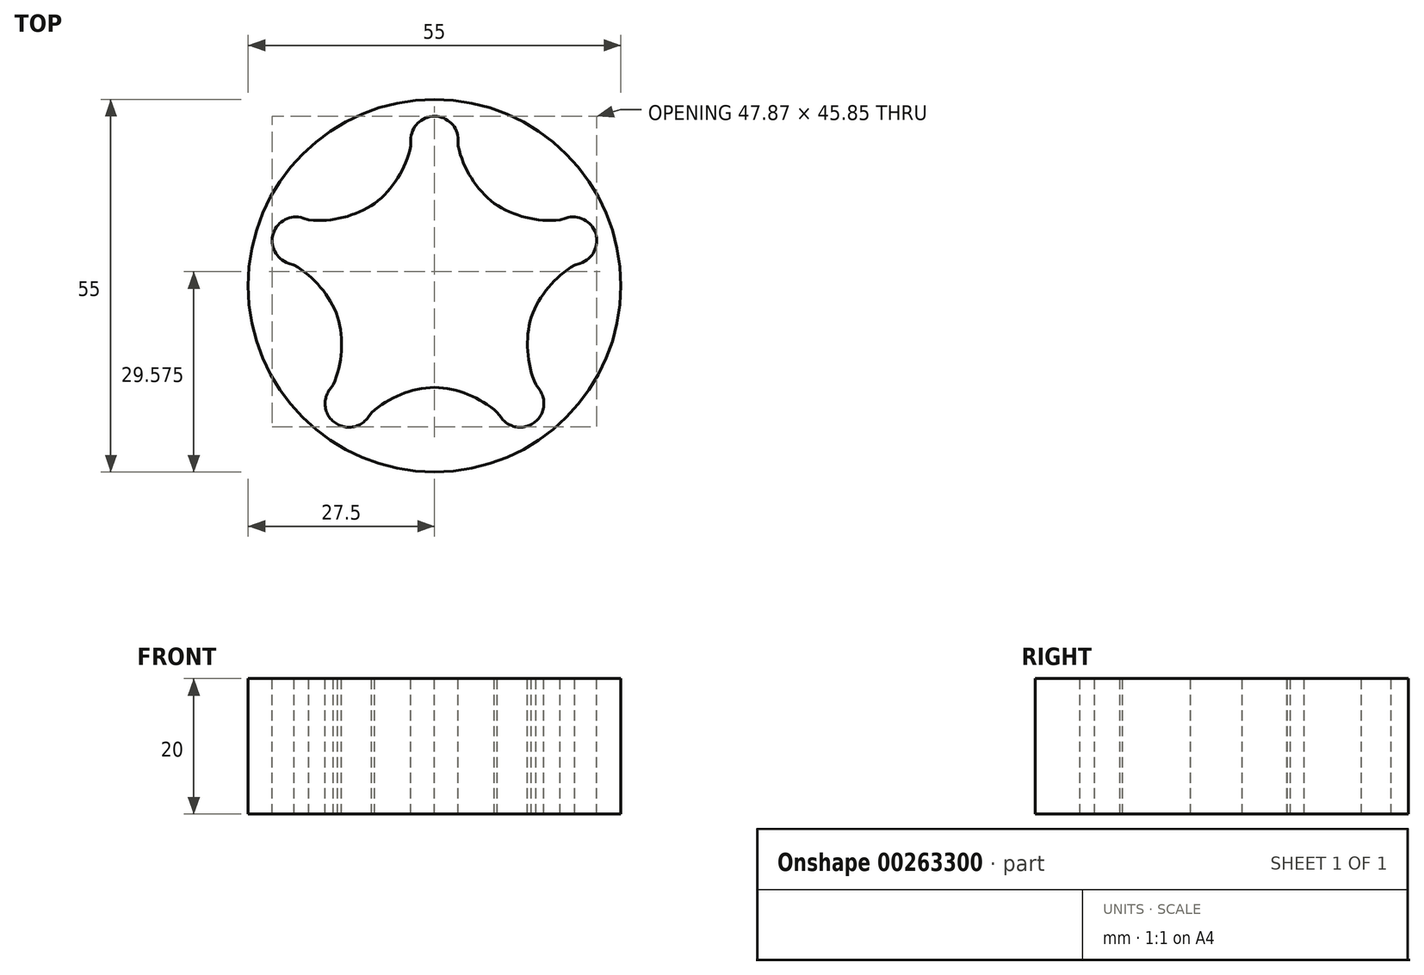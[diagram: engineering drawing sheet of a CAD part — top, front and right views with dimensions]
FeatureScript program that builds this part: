
annotation { "Feature Type Name" : "Feature", "Feature Type Description" : "" }
export const myFeature = defineFeature(function(context is Context, id is Id, definition is map)
    precondition{}
    {
        {
            var Q0;
            Q0=qCreatedBy(makeId("Top.planeOp"),FACE);
            var sketch = newSketch(context, id + "F0", { "sketchPlane" : qUnion([Q0])});
            skCircle(sketch, "E0", {"center": v(0, -5) * mm, "radius": 27.5 * mm});
            skLineSegment(sketch, "E1", {"start": v(0, -5) * mm, "end": v(-57.06, 13.54) * mm});
            skLineSegment(sketch, "E2", {"start": v(0, -5) * mm, "end": v(52.71, 12.13) * mm});
            skLineSegment(sketch, "E3", {"start": v(0, -5) * mm, "end": v(23.23, -36.98) * mm});
            skLineSegment(sketch, "E4", {"start": v(0, -5) * mm, "end": v(-21.37, -34.42) * mm});
            skPoint(sketch, "E5", {"position": v(0, 16.5) * mm});
            skArc(sketch, "E6", {"start": v(-3.5, 16.5) * mm, "mid": v(0, 20) * mm, "end": v(3.5, 16.5) * mm});
            skArc(sketch, "E7.MirrorCS", {"start": v(9.8, -24.45) * mm, "mid": v(14.7, -25.23) * mm, "end": v(15.47, -20.34) * mm});
            skArc(sketch, "E8.MirrorCS", {"start": v(-21.53, -1.68) * mm, "mid": v(-23.78, 2.73) * mm, "end": v(-19.37, 4.97) * mm});
            skArc(sketch, "E9.MirrorCS", {"start": v(21.53, -1.68) * mm, "mid": v(23.78, 2.73) * mm, "end": v(19.37, 4.97) * mm});
            skArc(sketch, "E10.MirrorCS", {"start": v(-9.8, -24.45) * mm, "mid": v(-14.7, -25.23) * mm, "end": v(-15.47, -20.34) * mm});
            skPoint(sketch, "E11", {"position": v(0, -20) * mm});
            skSolve(sketch);
        }
        {
            var Q0;
            Q0=qCreatedBy(makeId("Top.planeOp"),FACE);
            var sketch = newSketch(context, id + "F1", { "sketchPlane" : qUnion([Q0])});
            skPoint(sketch, "E12", {"position": v(0, -9.66) * mm});
            skPoint(sketch, "E13", {"position": v(11.67, -21.33) * mm});
            skPoint(sketch, "E14", {"position": v(-11.67, -21.33) * mm});
            skPoint(sketch, "E15.MirrorP", {"position": v(14.58, -9.74) * mm});
            skPoint(sketch, "E16", {"position": v(0, -20) * mm});
            skPoint(sketch, "E17", {"position": v(9.8, -24.45) * mm});
            skPoint(sketch, "E18", {"position": v(-9.8, -24.45) * mm});
            skPoint(sketch, "E19", {"position": v(-18.52, 4.7) * mm});
            skPoint(sketch, "E20", {"position": v(-8.82, 7.14) * mm});
            skArc(sketch, "E21", {"start": v(-18.52, 4.7) * mm, "mid": v(-13.46, 5.08) * mm, "end": v(-8.82, 7.14) * mm});
            skLineSegment(sketch, "E22", {"start": v(-18.52, 4.7) * mm, "end": v(-19.37, 4.97) * mm});
            skLineSegment(sketch, "E23.MirrorCS", {"start": v(-20.69, -1.96) * mm, "end": v(-21.53, -1.68) * mm});
            skArc(sketch, "E24.MirrorCS", {"start": v(-20.69, -1.96) * mm, "mid": v(-16.81, -5.24) * mm, "end": v(-14.27, -9.64) * mm});
            skArc(sketch, "E25.MirrorCS", {"start": v(9.29, -23.74) * mm, "mid": v(4.97, -21.06) * mm, "end": v(0, -20) * mm});
            skLineSegment(sketch, "E26.MirrorCS", {"start": v(9.29, -23.74) * mm, "end": v(9.8, -24.45) * mm});
            skArc(sketch, "E27.MirrorCS", {"start": v(-3.5, 15.61) * mm, "mid": v(-5.43, 10.92) * mm, "end": v(-8.82, 7.14) * mm});
            skLineSegment(sketch, "E28.MirrorCS", {"start": v(-3.5, 15.61) * mm, "end": v(-3.5, 16.5) * mm});
            skArc(sketch, "E29.MirrorCS", {"start": v(3.5, 15.61) * mm, "mid": v(5.43, 10.92) * mm, "end": v(8.82, 7.14) * mm});
            skArc(sketch, "E30.MirrorCS", {"start": v(18.52, 4.7) * mm, "mid": v(13.46, 5.08) * mm, "end": v(8.82, 7.14) * mm});
            skLineSegment(sketch, "E31.MirrorCS", {"start": v(18.52, 4.7) * mm, "end": v(19.37, 4.97) * mm});
            skLineSegment(sketch, "E32.MirrorCS", {"start": v(3.5, 15.61) * mm, "end": v(3.5, 16.5) * mm});
            skArc(sketch, "E33.MirrorCS", {"start": v(20.69, -1.96) * mm, "mid": v(16.81, -5.24) * mm, "end": v(14.27, -9.64) * mm});
            skArc(sketch, "E34.MirrorCS", {"start": v(14.95, -19.62) * mm, "mid": v(13.74, -14.69) * mm, "end": v(14.27, -9.64) * mm});
            skLineSegment(sketch, "E35.MirrorCS", {"start": v(14.95, -19.62) * mm, "end": v(15.47, -20.34) * mm});
            skLineSegment(sketch, "E36.MirrorCS", {"start": v(20.69, -1.96) * mm, "end": v(21.53, -1.68) * mm});
            skArc(sketch, "E37.MirrorCS", {"start": v(-14.95, -19.62) * mm, "mid": v(-13.74, -14.69) * mm, "end": v(-14.27, -9.64) * mm});
            skLineSegment(sketch, "E38.MirrorCS", {"start": v(-14.95, -19.62) * mm, "end": v(-15.47, -20.34) * mm});
            skArc(sketch, "E39.MirrorCS", {"start": v(-9.29, -23.74) * mm, "mid": v(-4.97, -21.06) * mm, "end": v(0, -20) * mm});
            skLineSegment(sketch, "E40.MirrorCS", {"start": v(-9.29, -23.74) * mm, "end": v(-9.8, -24.45) * mm});
            skArc(sketch, "E41", {"start": v(9.8, -24.45) * mm, "mid": v(14.7, -25.23) * mm, "end": v(15.47, -20.34) * mm});
            skArc(sketch, "E42", {"start": v(21.53, -1.68) * mm, "mid": v(23.78, 2.73) * mm, "end": v(19.37, 4.97) * mm});
            skArc(sketch, "E43", {"start": v(3.5, 16.5) * mm, "mid": v(0, 20) * mm, "end": v(-3.5, 16.5) * mm});
            skArc(sketch, "E44", {"start": v(-19.37, 4.97) * mm, "mid": v(-23.78, 2.73) * mm, "end": v(-21.53, -1.68) * mm});
            skArc(sketch, "E45", {"start": v(-15.47, -20.34) * mm, "mid": v(-14.7, -25.23) * mm, "end": v(-9.8, -24.45) * mm});
            skSolve(sketch);
        }
        {
            var Q0;
            Q0 = qSketchRegion(id + "F1", true);
            extrude(context, id + "F2", {"entities" : qUnion([Q0]), "depth" : 25 * mm});
        }
        {
            var Q0;
            {var subQ1=sQuery(id+"F0.wireOp",EDGE,"E1");var subQ6=makeQuery(id+"F0.imprint","IMPRINT",VERTEX,{"derivedFrom":subQ1});Q0=makeQuery(id+"F0.imprint","IMPRINT",FACE,{"disambiguationData":[TD([[makeQuery(id+"F0.imprint","IMPRINT",EDGE,{"disambiguationData":[TD([[subQ6,-1.0]])],"derivedFrom":subQ1}),1.0]])]});}
            var Q1;
            {var subQ1=sQuery(id+"F0.wireOp",EDGE,"E1");var subQ4=makeQuery(id+"F0.imprint","IMPRINT",VERTEX,{"derivedFrom":subQ1});Q1=makeQuery(id+"F0.imprint","IMPRINT",FACE,{"disambiguationData":[TD([[makeQuery(id+"F0.imprint","IMPRINT",EDGE,{"disambiguationData":[TD([[subQ4,-1.0]])],"derivedFrom":subQ1}),-1.0]])]});}
            var Q2;
            {var subQ1=sQuery(id+"F0.wireOp",EDGE,"E2");var subQ6=makeQuery(id+"F0.imprint","IMPRINT",VERTEX,{"derivedFrom":subQ1});Q2=makeQuery(id+"F0.imprint","IMPRINT",FACE,{"disambiguationData":[TD([[makeQuery(id+"F0.imprint","IMPRINT",EDGE,{"disambiguationData":[TD([[subQ6,-1.0]])],"derivedFrom":subQ1}),-1.0]])]});}
            var Q3;
            {var subQ0=sQuery(id+"F0.wireOp",EDGE,"E3");var subQ3=makeQuery(id+"F0.imprint","IMPRINT",VERTEX,{"derivedFrom":subQ0});Q3=makeQuery(id+"F0.imprint","IMPRINT",FACE,{"disambiguationData":[TD([[makeQuery(id+"F0.imprint","IMPRINT",EDGE,{"disambiguationData":[TD([[subQ3,-1.0]])],"derivedFrom":subQ0}),-1.0]])]});}
            extrude(context, id + "F3", {"entities" : qUnion([Q0, Q1, Q2, Q3]), "operationType" : NewBodyOperationType.ADD, "depth" : 20 * mm});
        }
        {
            var Q0;
            Q0=makeQuery(id+"F2.opExtrude","CAP_FACE",FACE,{"disambiguationData":[OSD([sQuery(id+"F1.wireOp",EDGE,"E23.MirrorCS"),sQuery(id+"F1.wireOp",EDGE,"E24.MirrorCS"),sQuery(id+"F1.wireOp",EDGE,"E25.MirrorCS"),sQuery(id+"F1.wireOp",EDGE,"E26.MirrorCS"),sQuery(id+"F1.wireOp",EDGE,"E29.MirrorCS"),sQuery(id+"F1.wireOp",EDGE,"E30.MirrorCS"),sQuery(id+"F1.wireOp",EDGE,"E31.MirrorCS"),sQuery(id+"F1.wireOp",EDGE,"E32.MirrorCS"),sQuery(id+"F1.wireOp",EDGE,"E33.MirrorCS"),sQuery(id+"F1.wireOp",EDGE,"E34.MirrorCS"),sQuery(id+"F1.wireOp",EDGE,"E35.MirrorCS"),sQuery(id+"F1.wireOp",EDGE,"E36.MirrorCS"),sQuery(id+"F1.wireOp",EDGE,"E21"),sQuery(id+"F1.wireOp",EDGE,"E27.MirrorCS"),sQuery(id+"F1.wireOp",EDGE,"E28.MirrorCS"),sQuery(id+"F1.wireOp",EDGE,"E22"),sQuery(id+"F1.wireOp",EDGE,"E37.MirrorCS"),sQuery(id+"F1.wireOp",EDGE,"E38.MirrorCS"),sQuery(id+"F1.wireOp",EDGE,"E39.MirrorCS"),sQuery(id+"F1.wireOp",EDGE,"E40.MirrorCS"),sQuery(id+"F1.wireOp",EDGE,"E41"),sQuery(id+"F1.wireOp",EDGE,"E42"),sQuery(id+"F1.wireOp",EDGE,"E43"),sQuery(id+"F1.wireOp",EDGE,"E44"),sQuery(id+"F1.wireOp",EDGE,"E45")])],"isStart":false});
            extrude(context, id + "F4", {"entities" : qUnion([Q0]), "operationType" : NewBodyOperationType.REMOVE, "oppositeDirection" : true, "depth" : 25 * mm});
        }
    });
